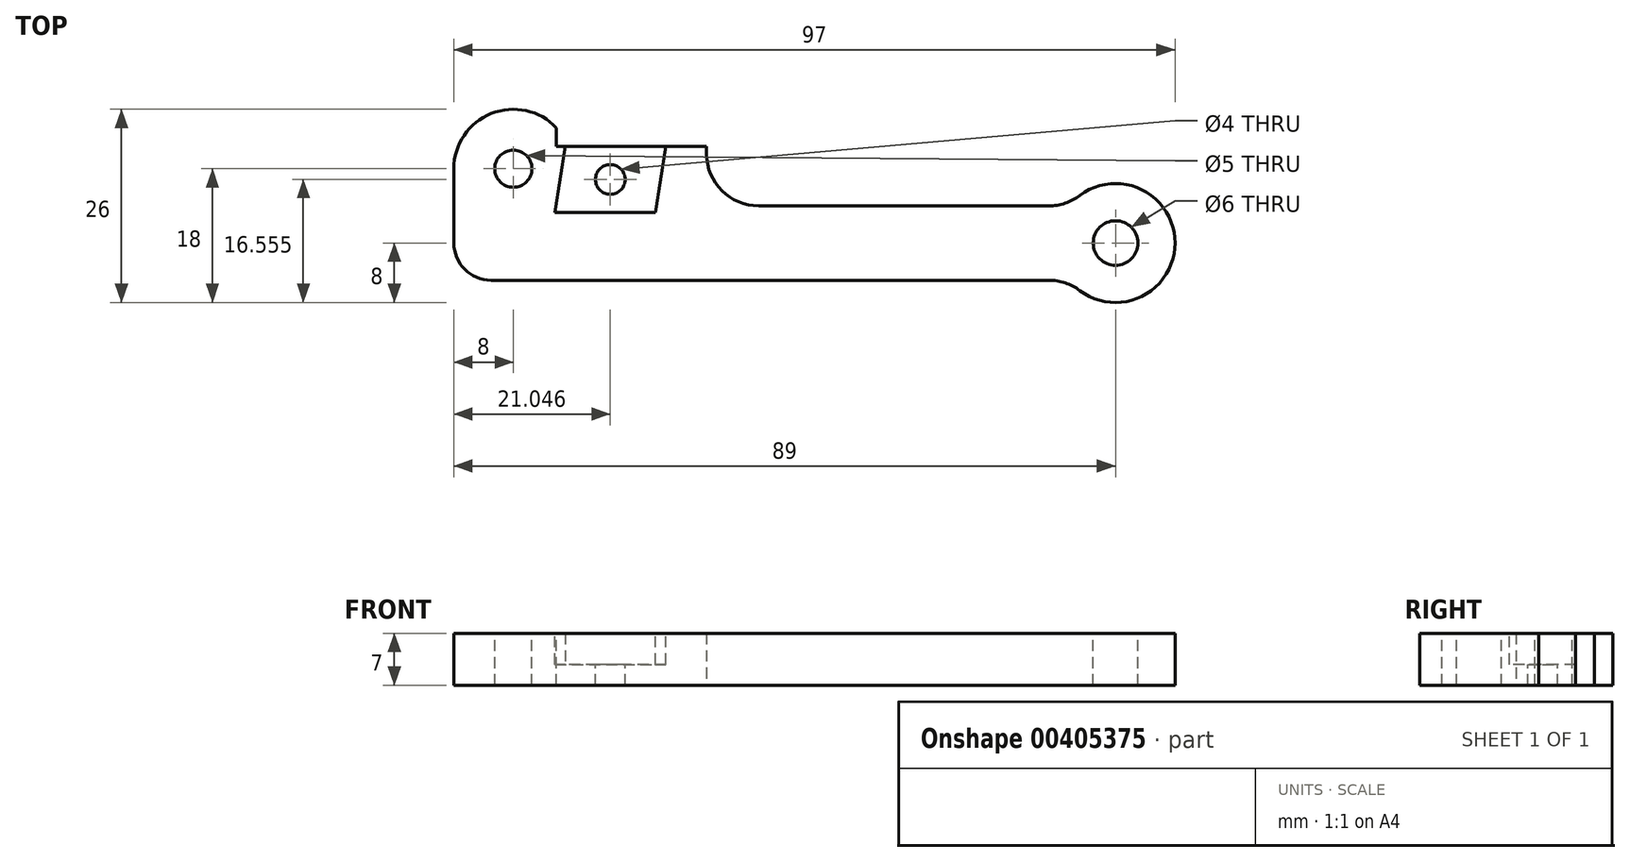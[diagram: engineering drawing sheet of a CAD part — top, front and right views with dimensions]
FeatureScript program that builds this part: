
annotation { "Feature Type Name" : "Feature", "Feature Type Description" : "" }
export const myFeature = defineFeature(function(context is Context, id is Id, definition is map)
    precondition{}
    {
        {
            var Q0;
            Q0=qCreatedBy(makeId("Top.planeOp"),FACE);
            var sketch = newSketch(context, id + "F0", { "sketchPlane" : qUnion([Q0])});
            skLineSegment(sketch, "E0.bottom", {"start": v(-17, 17) * mm, "end": v(-2, 17) * mm});
            skLineSegment(sketch, "E0.left", {"start": v(-17, 17) * mm, "end": v(-17, -10) * mm});
            skLineSegment(sketch, "E0.right", {"start": v(17, 8) * mm, "end": v(17, -10) * mm});
            skPoint(sketch, "E0.middle", {"position": v(0, 0) * mm});
            skLineSegment(sketch, "E1.top", {"start": v(17, 8) * mm, "end": v(-2, 8) * mm});
            skLineSegment(sketch, "E1.right", {"start": v(-2, 17) * mm, "end": v(-2, 8) * mm});
            skPoint(sketch, "E2.orphan", {"position": v(17, 17) * mm});
            skLineSegment(sketch, "E3", {"start": v(-17, -10) * mm, "end": v(17, -10) * mm});
            skPoint(sketch, "E0.top.start.orphan", {"position": v(-17, -17) * mm});
            skPoint(sketch, "E4.orphan", {"position": v(17, -17) * mm});
            skLineSegment(sketch, "E5.bottom", {"start": v(17, -10) * mm, "end": v(72, -10) * mm});
            skLineSegment(sketch, "E5.top", {"start": v(17, 0) * mm, "end": v(72, 0) * mm});
            skLineSegment(sketch, "E5.left", {"start": v(17, -10) * mm, "end": v(17, 0) * mm});
            skLineSegment(sketch, "E5.right", {"start": v(72, -10) * mm, "end": v(72, 0) * mm});
            skCircle(sketch, "E6", {"center": v(72, -5) * mm, "radius": 8 * mm});
            skSolve(sketch);
        }
        {
            var Q0;
            Q0=makeQuery(id+"F0.imprint","IMPRINT",FACE,{"disambiguationData":[TD([[makeQuery(id+"F0.imprint","IMPRINT",EDGE,{"derivedFrom":sQuery(id+"F0.wireOp",EDGE,"E0.bottom")}),-1.0]])]});
            var Q1;
            Q1=makeQuery(id+"F0.imprint","IMPRINT",FACE,{"disambiguationData":[TD([[makeQuery(id+"F0.imprint","IMPRINT",EDGE,{"derivedFrom":sQuery(id+"F0.wireOp",EDGE,"E5.bottom")}),1.0]])]});
            var Q2;
            Q2=makeQuery(id+"F0.imprint","IMPRINT",FACE,{"disambiguationData":[TD([[makeQuery(id+"F0.imprint","IMPRINT",EDGE,{"derivedFrom":sQuery(id+"F0.wireOp",EDGE,"E5.right")}),-1.0]])]});
            extrude(context, id + "F1", {"entities" : qUnion([Q0, Q1, Q2]), "depth" : 7 * mm});
        }
        {
            var Q0;
            Q0=makeQuery(id+"F1.opExtrude","CAP_FACE",FACE,{"disambiguationData":[OSD([sQuery(id+"F0.wireOp",EDGE,"E0.bottom"),sQuery(id+"F0.wireOp",EDGE,"E0.top"),sQuery(id+"F0.wireOp",EDGE,"E0.left"),sQuery(id+"F0.wireOp",EDGE,"E0.right"),sQuery(id+"F0.wireOp",EDGE,"E1.top"),sQuery(id+"F0.wireOp",EDGE,"E1.right")])],"isStart":false});
            var sketch = newSketch(context, id + "F2", { "sketchPlane" : qUnion([Q0])});
            skLineSegment(sketch, "E7", {"start": v(-2, 8) * mm, "end": v(-3.4, -0.89) * mm});
            skLineSegment(sketch, "E8", {"start": v(-3.4, -0.89) * mm, "end": v(10.1, -0.89) * mm});
            skLineSegment(sketch, "E9", {"start": v(10.1, -0.89) * mm, "end": v(11.5, 8) * mm});
            skLineSegment(sketch, "E10", {"start": v(-2.7, 3.56) * mm, "end": v(10.8, 3.56) * mm, "construction": true});
            skLineSegment(sketch, "E11", {"start": v(3.34, -0.89) * mm, "end": v(4.75, 8) * mm, "construction": true});
            skCircle(sketch, "E12", {"center": v(4.05, 3.56) * mm, "radius": 2 * mm});
            skSolve(sketch);
        }
        {
            var Q0;
            {var subQ0=sQuery(id+"F2.wireOp",EDGE,"E7");Q0=makeQuery(id+"F2.imprint","IMPRINT",FACE,{"disambiguationData":[TD([[makeQuery(id+"F2.imprint","IMPRINT",EDGE,{"derivedFrom":subQ0}),1.0]])]});}
            extrude(context, id + "F3", {"entities" : qUnion([Q0]), "operationType" : NewBodyOperationType.REMOVE, "oppositeDirection" : true, "depth" : 4.2 * mm});
        }
        {
            var Q0;
            Q0=makeQuery(id+"F3.boolean.opBoolean","SPLIT",FACE,{"disambiguationData":[TD([makeQuery(id+"F3.opExtrude","SWEPT_FACE",FACE,{"disambiguationData":[OSD([sQuery(id+"F2.wireOp",EDGE,"E12")])]})])],"derivedFrom":makeQuery(id+"F1.opExtrude","CAP_FACE",FACE,{"disambiguationData":[OSD([sQuery(id+"F0.wireOp",EDGE,"E0.bottom"),sQuery(id+"F0.wireOp",EDGE,"E0.top"),sQuery(id+"F0.wireOp",EDGE,"E0.left"),sQuery(id+"F0.wireOp",EDGE,"E0.right"),sQuery(id+"F0.wireOp",EDGE,"E1.top"),sQuery(id+"F0.wireOp",EDGE,"E1.right")])],"isStart":false})});
            extrude(context, id + "F4", {"entities" : qUnion([Q0]), "operationType" : NewBodyOperationType.REMOVE, "oppositeDirection" : true, "depth" : 25 * mm});
        }
        {
            var Q0;
            {var subQ0=sQuery(id+"F0.wireOp",EDGE,"E0.left");var subQ1=sQuery(id+"F0.wireOp",EDGE,"E0.top");var subQ2=sQuery(id+"F0.wireOp",EDGE,"E0.right");var subQ3=sQuery(id+"F0.wireOp",EDGE,"E0.bottom");var subQ4=sQuery(id+"F0.wireOp",EDGE,"E1.top");var subQ5=sQuery(id+"F0.wireOp",EDGE,"E1.right");Q0=makeQuery(id+"F3.boolean.opBoolean","SPLIT",FACE,{"disambiguationData":[TD([makeQuery(id+"F1.opExtrude","SWEPT_FACE",FACE,{"disambiguationData":[OSD([subQ3])]})])],"derivedFrom":makeQuery(id+"F1.opExtrude","CAP_FACE",FACE,{"disambiguationData":[OSD([subQ3,subQ1,subQ0,subQ2,subQ4,subQ5])],"isStart":false})});}
            var sketch = newSketch(context, id + "F5", { "sketchPlane" : qUnion([Q0])});
            skCircle(sketch, "E13", {"center": v(-9, 5) * mm, "radius": 2.5 * mm});
            skSolve(sketch);
        }
        {
            var Q0;
            Q0=makeQuery(id+"F5.imprint","IMPRINT",FACE,{"disambiguationData":[TD([[makeQuery(id+"F5.imprint","IMPRINT",EDGE,{"derivedFrom":sQuery(id+"F5.wireOp",EDGE,"E13")}),1.0]])]});
            extrude(context, id + "F6", {"entities" : qUnion([Q0]), "operationType" : NewBodyOperationType.REMOVE, "oppositeDirection" : true, "depth" : 25 * mm});
        }
        {
            var Q0;
            Q0=makeQuery(id+"F1.opExtrude","SWEPT_EDGE",EDGE,{"disambiguationData":[OSD([sQuery(id+"F0.wireOp",EDGE,"E0.bottom"),sQuery(id+"F0.wireOp",EDGE,"E0.left")])]});
            fillet(context, id + "F7", {"entities" : qUnion([Q0]), "radius" : 8 * mm, "tangentPropagation" : true, "allowEdgeOverflow" : false});
        }
        {
            var Q0;
            Q0=makeQuery(id+"F1.opExtrude","SWEPT_EDGE",EDGE,{"disambiguationData":[OSD([sQuery(id+"F0.wireOp",EDGE,"E0.left"),sQuery(id+"F0.wireOp",EDGE,"E3")])]});
            fillet(context, id + "F8", {"entities" : qUnion([Q0]), "radius" : 5 * mm, "tangentPropagation" : true, "allowEdgeOverflow" : false});
        }
        {
            var Q0;
            Q0=makeQuery(id+"F1.opExtrude","SWEPT_EDGE",EDGE,{"disambiguationData":[OSD([sQuery(id+"F0.wireOp",EDGE,"E0.bottom"),sQuery(id+"F0.wireOp",EDGE,"E1.right")])]});
            fillet(context, id + "F9", {"entities" : qUnion([Q0]), "radius" : 9 * mm, "tangentPropagation" : true, "allowEdgeOverflow" : false});
        }
        {
            var Q0;
            {var subQ0=sQuery(id+"F0.wireOp",EDGE,"E0.right");var subQ1=sQuery(id+"F0.wireOp",EDGE,"E5.right");var subQ2=sQuery(id+"F0.wireOp",EDGE,"E5.top");var subQ3=sQuery(id+"F0.wireOp",EDGE,"E5.bottom");var subQ4=sQuery(id+"F0.wireOp",EDGE,"E3");var subQ5=sQuery(id+"F0.wireOp",EDGE,"E1.right");var subQ6=sQuery(id+"F0.wireOp",EDGE,"E0.bottom");var subQ7=sQuery(id+"F0.wireOp",EDGE,"E1.top");var subQ8=sQuery(id+"F0.wireOp",EDGE,"E0.left");Q0=makeQuery(id+"F3.boolean.opBoolean","SPLIT",FACE,{"disambiguationData":[TD([makeQuery(id+"F1.opExtrude","SWEPT_FACE",FACE,{"disambiguationData":[OSD([subQ6])]})])],"derivedFrom":makeQuery(id+"F1.opExtrude","CAP_FACE",FACE,{"disambiguationData":[OSD([subQ6,subQ8,subQ0,subQ7,subQ5,subQ4,subQ3,subQ2,subQ1])],"isStart":false})});}
            var sketch = newSketch(context, id + "F10", { "sketchPlane" : qUnion([Q0])});
            skPoint(sketch, "E14.oppositeSnap0", {"position": v(-3.2, 13.84) * mm});
            skLineSegment(sketch, "E14.bottom", {"start": v(-2, 8) * mm, "end": v(-3.2, 8) * mm});
            skLineSegment(sketch, "E14.top", {"start": v(-2, 18) * mm, "end": v(-3.2, 18) * mm});
            skLineSegment(sketch, "E14.left", {"start": v(-2, 8) * mm, "end": v(-2, 18) * mm});
            skLineSegment(sketch, "E14.right", {"start": v(-3.2, 8) * mm, "end": v(-3.2, 18) * mm});
            skSolve(sketch);
        }
        {
            var Q0;
            {var subQ0=sQuery(id+"F10.wireOp",EDGE,"E14.top");Q0=makeQuery(id+"F10.imprint","IMPRINT",FACE,{"disambiguationData":[TD([[makeQuery(id+"F10.imprint","IMPRINT",EDGE,{"derivedFrom":subQ0}),1.0]])]});}
            var Q1;
            {var subQ0=sQuery(id+"F10.wireOp",EDGE,"E14.bottom");Q1=makeQuery(id+"F10.imprint","IMPRINT",FACE,{"disambiguationData":[TD([[makeQuery(id+"F10.imprint","IMPRINT",EDGE,{"derivedFrom":subQ0}),-1.0]])]});}
            extrude(context, id + "F11", {"entities" : qUnion([Q0, Q1]), "operationType" : NewBodyOperationType.REMOVE, "oppositeDirection" : true, "depth" : 25 * mm});
        }
        {
            var Q0;
            {var subQ0=sQuery(id+"F0.wireOp",EDGE,"E0.right");var subQ1=sQuery(id+"F0.wireOp",EDGE,"E5.right");var subQ2=sQuery(id+"F0.wireOp",EDGE,"E5.top");var subQ3=sQuery(id+"F0.wireOp",EDGE,"E5.bottom");var subQ4=sQuery(id+"F0.wireOp",EDGE,"E3");var subQ5=sQuery(id+"F0.wireOp",EDGE,"E1.right");var subQ6=sQuery(id+"F0.wireOp",EDGE,"E0.bottom");var subQ7=sQuery(id+"F0.wireOp",EDGE,"E1.top");var subQ8=sQuery(id+"F0.wireOp",EDGE,"E0.left");Q0=makeQuery(id+"F3.boolean.opBoolean","SPLIT",FACE,{"disambiguationData":[TD([makeQuery(id+"F1.opExtrude","SWEPT_FACE",FACE,{"disambiguationData":[OSD([subQ6])]})])],"derivedFrom":makeQuery(id+"F1.opExtrude","CAP_FACE",FACE,{"disambiguationData":[OSD([subQ6,subQ8,subQ0,subQ7,subQ5,subQ4,subQ3,subQ2,subQ1])],"isStart":false})});}
            var sketch = newSketch(context, id + "F12", { "sketchPlane" : qUnion([Q0])});
            skCircle(sketch, "E15", {"center": v(-9, 5) * mm, "radius": 8 * mm});
            skSolve(sketch);
        }
        {
            var Q0;
            {var subQ12=makeQuery(id+"F11.boolean.opBoolean","COPY",EDGE,{"derivedFrom":makeQuery(id+"F11.opExtrude","CAP_EDGE",EDGE,{"disambiguationData":[OSD([sQuery(id+"F10.wireOp",EDGE,"E14.right")])],"isStart":true})});var subQ13=sQuery(id+"F12.wireOp",EDGE,"E15");var subQ14=makeQuery(id+"F12.imprint","INTERSECT",VERTEX,{"derivedFrom":[subQ12,subQ13]});Q0=makeQuery(id+"F12.imprint","IMPRINT",FACE,{"disambiguationData":[TD([[makeQuery(id+"F12.imprint","IMPRINT",EDGE,{"disambiguationData":[TD([[subQ14,-1.0]])],"derivedFrom":subQ13}),-1.0]])]});}
            extrude(context, id + "F13", {"entities" : qUnion([Q0]), "operationType" : NewBodyOperationType.REMOVE, "oppositeDirection" : true, "depth" : 25 * mm});
        }
        {
            var Q0;
            {var subQ0=sQuery(id+"F0.wireOp",EDGE,"E0.right");var subQ1=sQuery(id+"F0.wireOp",EDGE,"E5.right");var subQ2=sQuery(id+"F0.wireOp",EDGE,"E5.top");var subQ3=sQuery(id+"F0.wireOp",EDGE,"E5.bottom");var subQ4=sQuery(id+"F0.wireOp",EDGE,"E3");var subQ5=sQuery(id+"F0.wireOp",EDGE,"E1.right");var subQ6=sQuery(id+"F0.wireOp",EDGE,"E0.bottom");var subQ7=sQuery(id+"F0.wireOp",EDGE,"E1.top");var subQ8=sQuery(id+"F0.wireOp",EDGE,"E0.left");Q0=makeQuery(id+"F3.boolean.opBoolean","SPLIT",FACE,{"disambiguationData":[TD([makeQuery(id+"F1.opExtrude","SWEPT_FACE",FACE,{"disambiguationData":[OSD([subQ6])]})])],"derivedFrom":makeQuery(id+"F1.opExtrude","CAP_FACE",FACE,{"disambiguationData":[OSD([subQ6,subQ8,subQ0,subQ7,subQ5,subQ4,subQ3,subQ2,subQ1])],"isStart":false})});}
            var sketch = newSketch(context, id + "F14", { "sketchPlane" : qUnion([Q0])});
            skCircle(sketch, "E16", {"center": v(72, -5) * mm, "radius": 3 * mm});
            skSolve(sketch);
        }
        {
            var Q0;
            Q0=makeQuery(id+"F14.imprint","IMPRINT",FACE,{"disambiguationData":[TD([[makeQuery(id+"F14.imprint","IMPRINT",EDGE,{"derivedFrom":sQuery(id+"F14.wireOp",EDGE,"vYPmPg8h-xr6M-HVMS-aRUW-gpzYCpgHTlGM")}),1.0]])]});
            var Q1;
            Q1=makeQuery(id+"F14.imprint","IMPRINT",FACE,{"disambiguationData":[TD([[makeQuery(id+"F14.imprint","IMPRINT",EDGE,{"derivedFrom":sQuery(id+"F14.wireOp",EDGE,"E16")}),1.0]])]});
            extrude(context, id + "F15", {"entities" : qUnion([Q0, Q1]), "operationType" : NewBodyOperationType.REMOVE, "oppositeDirection" : true, "depth" : 25 * mm});
        }
        {
            var Q0;
            Q0=makeQuery(id+"F1.opExtrude","SWEPT_EDGE",EDGE,{"disambiguationData":[OSD([sQuery(id+"F0.wireOp",EDGE,"E0.right"),sQuery(id+"F0.wireOp",EDGE,"E5.top"),sQuery(id+"F0.wireOp",EDGE,"E5.left")])]});
            var Q1;
            Q1=makeQuery(id+"F1.opExtrude","SWEPT_EDGE",EDGE,{"disambiguationData":[OSD([sQuery(id+"F0.wireOp",EDGE,"E5.bottom"),sQuery(id+"F0.wireOp",EDGE,"E6")])]});
            var Q2;
            Q2=makeQuery(id+"F1.opExtrude","SWEPT_EDGE",EDGE,{"disambiguationData":[OSD([sQuery(id+"F0.wireOp",EDGE,"E5.top"),sQuery(id+"F0.wireOp",EDGE,"E6")])]});
            fillet(context, id + "F16", {"entities" : qUnion([Q0, Q1, Q2]), "radius" : 7 * mm, "tangentPropagation" : true, "allowEdgeOverflow" : false});
        }
    });
